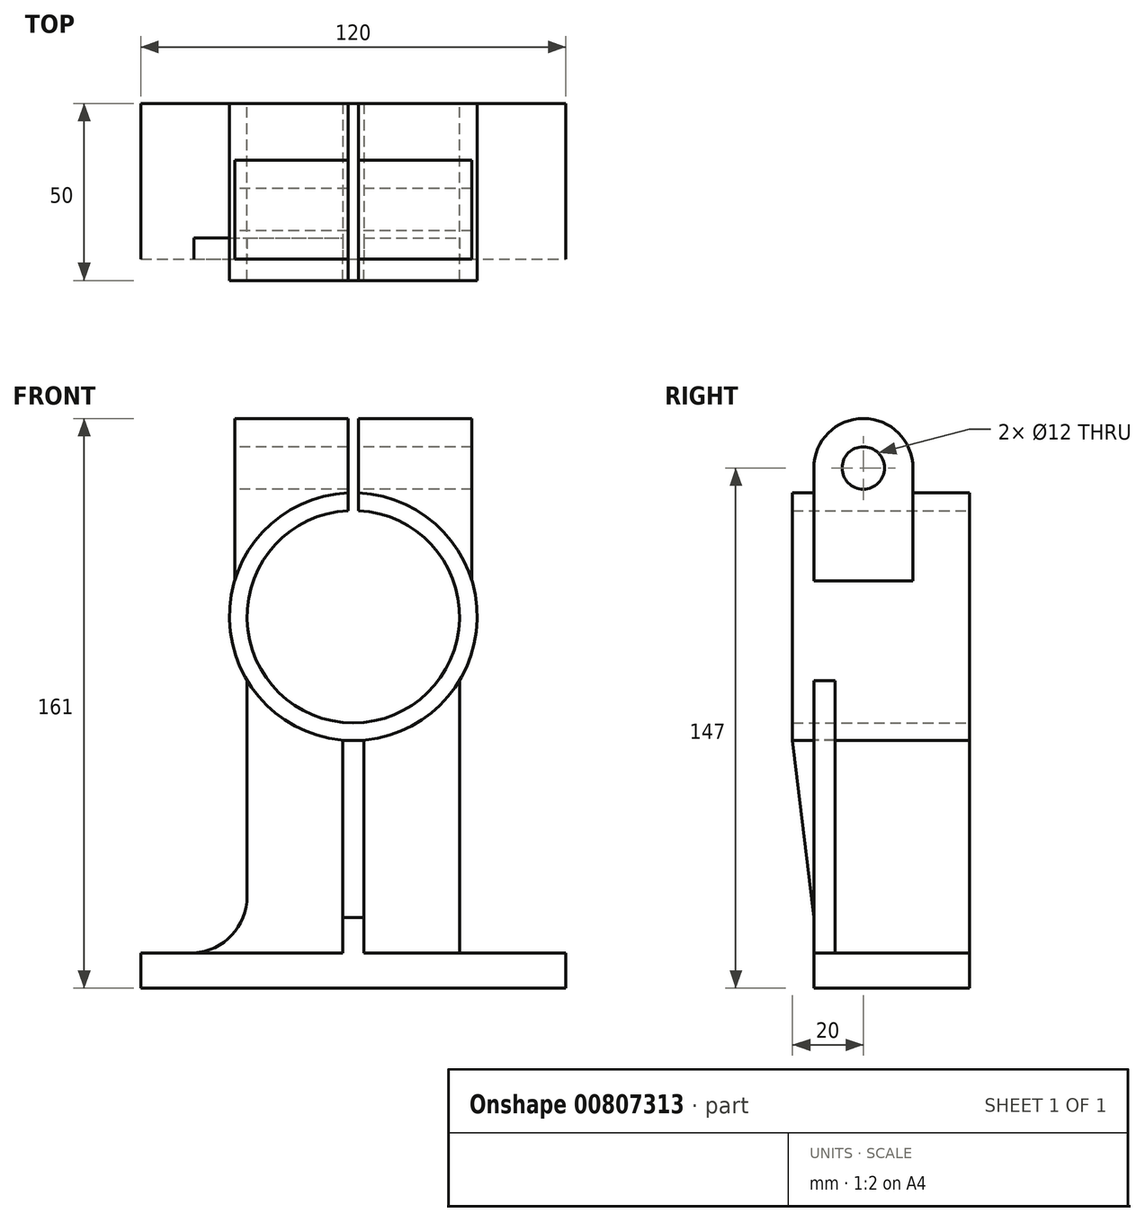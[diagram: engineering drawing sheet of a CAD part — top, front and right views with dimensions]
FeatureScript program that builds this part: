
annotation { "Feature Type Name" : "Feature", "Feature Type Description" : "" }
export const myFeature = defineFeature(function(context is Context, id is Id, definition is map)
    precondition{}
    {
        {
            var Q0;
            Q0=qCreatedBy(makeId("Front.planeOp"),FACE);
            var sketch = newSketch(context, id + "F0", { "sketchPlane" : qUnion([Q0])});
            skLineSegment(sketch, "E0", {"start": v(0, 86.34) * mm, "end": v(0, -230.36) * mm, "construction": true});
            skLineSegment(sketch, "E1", {"start": v(-112.36, 0) * mm, "end": v(131.8, 0) * mm, "construction": true});
            skLineSegment(sketch, "E2", {"start": v(-30, -35) * mm, "end": v(30, -35) * mm});
            skPoint(sketch, "E3", {"position": v(0, -35) * mm});
            skLineSegment(sketch, "E4", {"start": v(-60, -105) * mm, "end": v(60, -105) * mm});
            skPoint(sketch, "E5", {"position": v(0, -105) * mm});
            skLineSegment(sketch, "E6", {"start": v(-30, -35) * mm, "end": v(-30, -95) * mm});
            skLineSegment(sketch, "E7", {"start": v(30, -35) * mm, "end": v(30, -95) * mm});
            skLineSegment(sketch, "E8", {"start": v(-60, -105) * mm, "end": v(-60, -95) * mm});
            skLineSegment(sketch, "E9", {"start": v(60, -95) * mm, "end": v(60, -105) * mm});
            skLineSegment(sketch, "E10", {"start": v(-30, -35) * mm, "end": v(-30, -18.03) * mm});
            skLineSegment(sketch, "E11", {"start": v(30, -35) * mm, "end": v(30, -18.03) * mm});
            skLineSegment(sketch, "E12", {"start": v(-3, -85) * mm, "end": v(3, -85) * mm});
            skPoint(sketch, "E13", {"position": v(0, -85) * mm});
            skLineSegment(sketch, "E14", {"start": v(-3, -85) * mm, "end": v(-3, -34.87) * mm});
            skLineSegment(sketch, "E15", {"start": v(3, -85) * mm, "end": v(3, -34.87) * mm});
            skLineSegment(sketch, "E16", {"start": v(-60, -95) * mm, "end": v(-30, -95) * mm});
            skLineSegment(sketch, "E17", {"start": v(-30, -95) * mm, "end": v(30, -95) * mm});
            skLineSegment(sketch, "E18", {"start": v(60, -95) * mm, "end": v(30, -95) * mm});
            skArc(sketch, "E19", {"start": v(-45, -95) * mm, "mid": v(-34.34, -89.99) * mm, "end": v(-30, -79.03) * mm});
            skArc(sketch, "E20.MirrorCS", {"start": v(45, -95) * mm, "mid": v(34.34, -89.99) * mm, "end": v(30, -79.03) * mm});
            skLineSegment(sketch, "E21", {"start": v(-1.5, 29.96) * mm, "end": v(1.5, 29.96) * mm, "construction": true});
            skPoint(sketch, "E22", {"position": v(0, 29.96) * mm});
            skArc(sketch, "E23", {"start": v(-1.5, 29.96) * mm, "mid": v(0, -30) * mm, "end": v(1.5, 29.96) * mm});
            skArc(sketch, "E24", {"start": v(1.5, 29.96) * mm, "mid": v(0, 30) * mm, "end": v(-1.5, 29.96) * mm});
            skLineSegment(sketch, "E25", {"start": v(-1.5, 29.96) * mm, "end": v(-1.5, 34.97) * mm});
            skLineSegment(sketch, "E26", {"start": v(1.5, 29.96) * mm, "end": v(1.5, 34.97) * mm});
            skArc(sketch, "E27", {"start": v(-1.5, 34.97) * mm, "mid": v(0, -35) * mm, "end": v(1.5, 34.97) * mm});
            skArc(sketch, "E28", {"start": v(1.5, 34.97) * mm, "mid": v(0, 35) * mm, "end": v(-1.5, 34.97) * mm, "construction": true});
            skPoint(sketch, "E29", {"position": v(0, 56) * mm});
            skLineSegment(sketch, "E30", {"start": v(-33.5, 56) * mm, "end": v(-33.5, 10.14) * mm});
            skLineSegment(sketch, "E31", {"start": v(33.5, 56) * mm, "end": v(33.5, 10.14) * mm});
            skLineSegment(sketch, "E32", {"start": v(-1.5, 34.97) * mm, "end": v(-1.5, 56) * mm});
            skLineSegment(sketch, "E33", {"start": v(1.5, 34.97) * mm, "end": v(1.5, 56) * mm});
            skLineSegment(sketch, "E34", {"start": v(-33.5, 56) * mm, "end": v(-1.5, 56) * mm});
            skLineSegment(sketch, "E35", {"start": v(1.5, 56) * mm, "end": v(33.5, 56) * mm});
            skLineSegment(sketch, "E36", {"start": v(-3, -85) * mm, "end": v(-3, -95) * mm});
            skLineSegment(sketch, "E37", {"start": v(3, -85) * mm, "end": v(3, -95) * mm});
            skSolve(sketch);
        }
        {
            var Q0;
            Q0=makeQuery(id+"F0.imprint","IMPRINT",FACE,{"disambiguationData":[TD([[makeQuery(id+"F0.imprint","IMPRINT",EDGE,{"derivedFrom":sQuery(id+"F0.wireOp",EDGE,"E23")}),-1.0]])]});
            var Q1;
            {var subQ1=sQuery(id+"F0.wireOp",EDGE,"E12");Q1=makeQuery(id+"F0.imprint","IMPRINT",FACE,{"disambiguationData":[TD([[makeQuery(id+"F0.imprint","IMPRINT",EDGE,{"derivedFrom":subQ1}),1.0]])]});}
            extrude(context, id + "F1", {"entities" : qUnion([Q0, Q1]), "depth" : 6 * mm, "offsetDistance" : 25 * mm});
        }
        {
            var Q0;
            Q0=makeQuery(id+"F0.imprint","IMPRINT",FACE,{"disambiguationData":[TD([[makeQuery(id+"F0.imprint","IMPRINT",EDGE,{"derivedFrom":sQuery(id+"F0.wireOp",EDGE,"E23")}),-1.0]])]});
            var Q1;
            {var subQ1=sQuery(id+"F0.wireOp",EDGE,"E12");Q1=makeQuery(id+"F0.imprint","IMPRINT",FACE,{"disambiguationData":[TD([[makeQuery(id+"F0.imprint","IMPRINT",EDGE,{"derivedFrom":subQ1}),1.0]])]});}
            var Q2;
            Q2=makeQuery(id+"F0.imprint","IMPRINT",FACE,{"disambiguationData":[TD([[makeQuery(id+"F0.imprint","IMPRINT",EDGE,{"derivedFrom":sQuery(id+"F0.wireOp",EDGE,"E4")}),1.0]])]});
            var Q3;
            Q3=makeQuery(id+"F0.imprint","IMPRINT",FACE,{"disambiguationData":[TD([[makeQuery(id+"F0.imprint","IMPRINT",EDGE,{"derivedFrom":sQuery(id+"F0.wireOp",EDGE,"E12")}),-1.0]])]});
            extrude(context, id + "F2", {"entities" : qUnion([Q0, Q1, Q2, Q3]), "oppositeDirection" : true, "depth" : 44 * mm, "offsetDistance" : 25 * mm});
        }
        {
            var Q0;
            {var subQ0=sQuery(id+"F0.wireOp",EDGE,"E10");Q0=makeQuery(id+"F0.imprint","IMPRINT",FACE,{"disambiguationData":[TD([[makeQuery(id+"F0.imprint","IMPRINT",EDGE,{"derivedFrom":subQ0}),-1.0]])]});}
            var Q1;
            {var subQ0=sQuery(id+"F0.wireOp",EDGE,"E11");Q1=makeQuery(id+"F0.imprint","IMPRINT",FACE,{"disambiguationData":[TD([[makeQuery(id+"F0.imprint","IMPRINT",EDGE,{"derivedFrom":subQ0}),1.0]])]});}
            var Q2;
            {var subQ3=sQuery(id+"F0.wireOp",EDGE,"E19");Q2=makeQuery(id+"F0.imprint","IMPRINT",FACE,{"disambiguationData":[TD([[makeQuery(id+"F0.imprint","IMPRINT",EDGE,{"derivedFrom":subQ3}),-1.0]])]});}
            var Q3;
            {var subQ3=sQuery(id+"F0.wireOp",EDGE,"E20.MirrorCS");Q3=makeQuery(id+"F0.imprint","IMPRINT",FACE,{"disambiguationData":[TD([[makeQuery(id+"F0.imprint","IMPRINT",EDGE,{"derivedFrom":subQ3}),1.0]])]});}
            var Q4;
            {var subQ0=sQuery(id+"F0.wireOp",EDGE,"E36");Q4=makeQuery(id+"F0.imprint","IMPRINT",FACE,{"disambiguationData":[TD([[makeQuery(id+"F0.imprint","IMPRINT",EDGE,{"derivedFrom":subQ0}),-1.0]])]});}
            var Q5;
            {var subQ0=sQuery(id+"F0.wireOp",EDGE,"E37");Q5=makeQuery(id+"F0.imprint","IMPRINT",FACE,{"disambiguationData":[TD([[makeQuery(id+"F0.imprint","IMPRINT",EDGE,{"derivedFrom":subQ0}),1.0]])]});}
            extrude(context, id + "F3", {"entities" : qUnion([Q0, Q1, Q2, Q3, Q4, Q5]), "oppositeDirection" : true, "depth" : 6 * mm, "offsetDistance" : 25 * mm});
        }
        {
            var Q0;
            {var subQ2=sQuery(id+"F0.wireOp",EDGE,"E30");Q0=makeQuery(id+"F0.imprint","IMPRINT",FACE,{"disambiguationData":[TD([[makeQuery(id+"F0.imprint","IMPRINT",EDGE,{"derivedFrom":subQ2}),1.0]])]});}
            var Q1;
            {var subQ2=sQuery(id+"F0.wireOp",EDGE,"E31");Q1=makeQuery(id+"F0.imprint","IMPRINT",FACE,{"disambiguationData":[TD([[makeQuery(id+"F0.imprint","IMPRINT",EDGE,{"derivedFrom":subQ2}),-1.0]])]});}
            extrude(context, id + "F4", {"entities" : qUnion([Q0, Q1]), "operationType" : NewBodyOperationType.ADD, "oppositeDirection" : true, "depth" : 28 * mm, "offsetDistance" : 25 * mm});
        }
        {
            var Q0;
            Q0=makeQuery(id+"F4.opExtrude","SWEPT_FACE",FACE,{"disambiguationData":[OSD([sQuery(id+"F0.wireOp",EDGE,"E30")])]});
            var sketch = newSketch(context, id + "F5", { "sketchPlane" : qUnion([Q0])});
            skLineSegment(sketch, "E38", {"start": v(-28, 42) * mm, "end": v(0, 42) * mm});
            skLineSegment(sketch, "E39.0", {"start": v(-28, 10.14) * mm, "end": v(0, 10.14) * mm});
            skLineSegment(sketch, "E40.0", {"start": v(-28, 56) * mm, "end": v(-28, 10.14) * mm});
            skLineSegment(sketch, "E41.0", {"start": v(0, 56) * mm, "end": v(0, 10.14) * mm});
            skPoint(sketch, "E42", {"position": v(-14, 42) * mm});
            skArc(sketch, "E43", {"start": v(-28, 42) * mm, "mid": v(-14, 56) * mm, "end": v(0, 42) * mm});
            skCircle(sketch, "E44", {"center": v(-14, 42) * mm, "radius": 6 * mm});
            skLineSegment(sketch, "E45.0", {"start": v(6, -85) * mm, "end": v(6, -35) * mm});
            skLineSegment(sketch, "E46.0", {"start": v(6, -85) * mm, "end": v(0, -85) * mm});
            skLineSegment(sketch, "E47.0", {"start": v(0, -85) * mm, "end": v(0, -34.87) * mm});
            skLineSegment(sketch, "E48.0", {"start": v(6, -35) * mm, "end": v(0, -35) * mm});
            skLineSegment(sketch, "E49", {"start": v(6, -35) * mm, "end": v(0, -85) * mm});
            skSolve(sketch);
        }
        {
            var Q0;
            {var subQ0=sQuery(id+"F5.wireOp",EDGE,"E40.0");var subQ1=makeQuery(id+"F4.opExtrude","SWEPT_EDGE",EDGE,{"disambiguationData":[OSD([sQuery(id+"F0.wireOp",EDGE,"E30"),sQuery(id+"F0.wireOp",EDGE,"E34")])]});var subQ2=makeQuery(id+"F5.imprint","INTERSECT",VERTEX,{"derivedFrom":[subQ1,subQ0]});Q0=makeQuery(id+"F5.imprint","IMPRINT",FACE,{"disambiguationData":[TD([[makeQuery(id+"F5.imprint","IMPRINT",EDGE,{"disambiguationData":[TD([[subQ2,-1.0]])],"derivedFrom":subQ0}),1.0]])]});}
            var Q1;
            {var subQ0=sQuery(id+"F5.wireOp",EDGE,"E41.0");var subQ1=makeQuery(id+"F4.opExtrude","SWEPT_EDGE",EDGE,{"disambiguationData":[OSD([sQuery(id+"F0.wireOp",EDGE,"E30"),sQuery(id+"F0.wireOp",EDGE,"E34")])]});var subQ2=makeQuery(id+"F5.imprint","INTERSECT",VERTEX,{"derivedFrom":[subQ1,subQ0]});Q1=makeQuery(id+"F5.imprint","IMPRINT",FACE,{"disambiguationData":[TD([[makeQuery(id+"F5.imprint","IMPRINT",EDGE,{"disambiguationData":[TD([[subQ2,-1.0]])],"derivedFrom":subQ0}),-1.0]])]});}
            var Q2;
            {var subQ0=sQuery(id+"F5.wireOp",EDGE,"E44");var subQ1=sQuery(id+"F5.wireOp",EDGE,"E38");var subQ2=makeQuery(id+"F5.imprint","INTERSECT",VERTEX,{"disambiguationData":[OD(0.0)],"derivedFrom":[subQ1,subQ0]});Q2=makeQuery(id+"F5.imprint","IMPRINT",FACE,{"disambiguationData":[TD([[makeQuery(id+"F5.imprint","IMPRINT",EDGE,{"disambiguationData":[TD([[subQ2,-1.0]])],"derivedFrom":subQ1}),1.0]])]});}
            var Q3;
            {var subQ0=sQuery(id+"F5.wireOp",EDGE,"E44");var subQ1=sQuery(id+"F5.wireOp",EDGE,"E38");var subQ2=makeQuery(id+"F5.imprint","INTERSECT",VERTEX,{"disambiguationData":[OD(0.0)],"derivedFrom":[subQ1,subQ0]});Q3=makeQuery(id+"F5.imprint","IMPRINT",FACE,{"disambiguationData":[TD([[makeQuery(id+"F5.imprint","IMPRINT",EDGE,{"disambiguationData":[TD([[subQ2,-1.0]])],"derivedFrom":subQ1}),-1.0]])]});}
            var Q4;
            Q4=makeQuery(id+"F5.imprint","IMPRINT",FACE,{"disambiguationData":[TD([[makeQuery(id+"F5.imprint","IMPRINT",EDGE,{"derivedFrom":sQuery(id+"F5.wireOp",EDGE,"E45.0")}),1.0]])]});
            extrude(context, id + "F6", {"entities" : qUnion([Q0, Q1, Q2, Q3, Q4]), "operationType" : NewBodyOperationType.REMOVE, "endBound" : BoundingType.THROUGH_ALL, "oppositeDirection" : true, "depth" : 25 * mm, "offsetDistance" : 25 * mm});
        }
        {
            var Q0;
            Q0=makeQuery(id+"F5.imprint","IMPRINT",FACE,{"disambiguationData":[TD([[makeQuery(id+"F5.imprint","IMPRINT",EDGE,{"derivedFrom":sQuery(id+"F5.wireOp",EDGE,"E45.0")}),1.0]])]});
            extrude(context, id + "F7", {"entities" : qUnion([Q0]), "operationType" : NewBodyOperationType.REMOVE, "endBound" : BoundingType.THROUGH_ALL, "oppositeDirection" : true, "depth" : 25 * mm, "offsetDistance" : 25 * mm});
        }
    });
